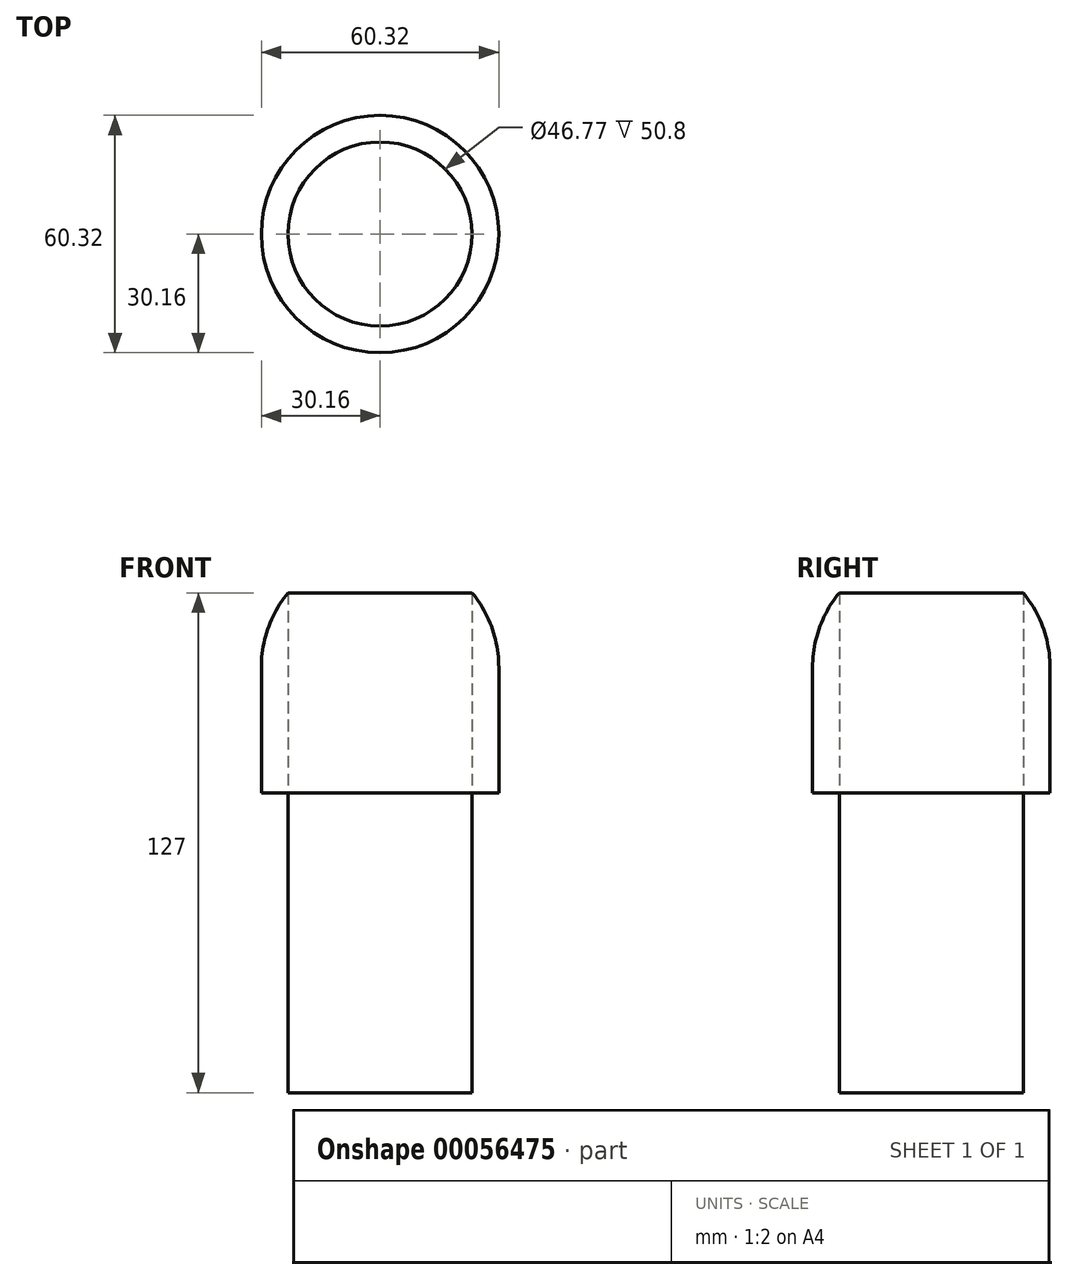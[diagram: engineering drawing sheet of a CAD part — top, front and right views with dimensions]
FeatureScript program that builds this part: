
annotation { "Feature Type Name" : "Feature", "Feature Type Description" : "" }
export const myFeature = defineFeature(function(context is Context, id is Id, definition is map)
    precondition{}
    {
        {
            var Q0;
            Q0=qCreatedBy(makeId("Top.planeOp"),FACE);
            var sketch = newSketch(context, id + "F0", { "sketchPlane" : qUnion([Q0])});
            skCircle(sketch, "E0", {"center": v(0, 0) * mm, "radius": 23.39 * mm});
            skSolve(sketch);
        }
        {
            var Q0;
            Q0=makeQuery(id+"F0.imprint","IMPRINT",FACE,{"disambiguationData":[TD([[makeQuery(id+"F0.imprint","IMPRINT",EDGE,{"derivedFrom":sQuery(id+"F0.wireOp",EDGE,"E0")}),1.0]])]});
            extrude(context, id + "F1", {"entities" : qUnion([Q0]), "depth" : 76.2 * mm});
        }
        {
            var Q0;
            Q0=makeQuery(id+"F1.opExtrude","CAP_FACE",FACE,{"disambiguationData":[OSD([sQuery(id+"F0.wireOp",EDGE,"E0")])],"isStart":false});
            var sketch = newSketch(context, id + "F2", { "sketchPlane" : qUnion([Q0])});
            skCircle(sketch, "E1", {"center": v(0, 0) * mm, "radius": 30.16 * mm});
            skSolve(sketch);
        }
        {
            var Q0;
            Q0=makeQuery(id+"F2.imprint","IMPRINT",FACE,{"disambiguationData":[TD([[makeQuery(id+"F2.imprint","IMPRINT",EDGE,{"derivedFrom":sQuery(id+"F2.wireOp",EDGE,"E1")}),1.0]])]});
            extrude(context, id + "F3", {"entities" : qUnion([Q0]), "depth" : 50.8 * mm});
        }
        {
            var Q0;
            Q0=makeQuery(id+"F1.opExtrude","CAP_FACE",FACE,{"disambiguationData":[OSD([sQuery(id+"F0.wireOp",EDGE,"E0")])],"isStart":false});
            extrude(context, id + "F4", {"entities" : qUnion([Q0]), "depth" : 50.8 * mm});
        }
        {
            var Q0;
            Q0=makeQuery(id+"F3.opExtrude","CAP_EDGE",EDGE,{"disambiguationData":[OSD([sQuery(id+"F2.wireOp",EDGE,"E1")])],"isStart":false});
            fillet(context, id + "F5", {"entities" : qUnion([Q0]), "radius" : 29.97 * mm, "tangentPropagation" : true, "allowEdgeOverflow" : false});
        }
    });
